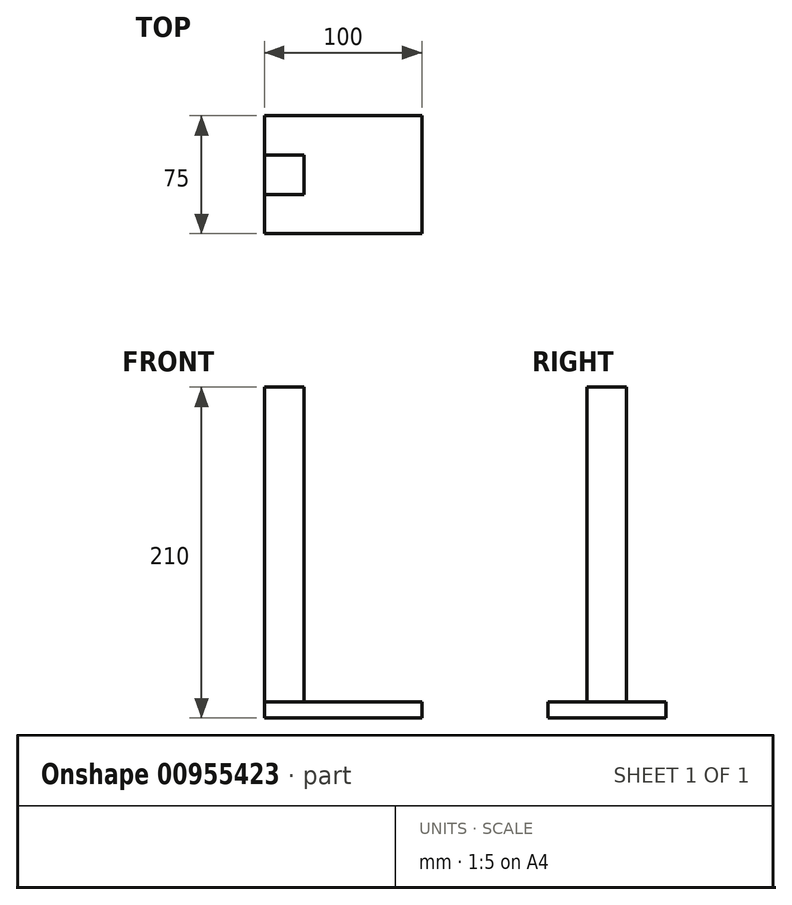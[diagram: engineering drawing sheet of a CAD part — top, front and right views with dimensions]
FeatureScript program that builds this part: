
annotation { "Feature Type Name" : "Feature", "Feature Type Description" : "" }
export const myFeature = defineFeature(function(context is Context, id is Id, definition is map)
    precondition{}
    {
        {
            var Q0;
            Q0=qCreatedBy(makeId("Top.planeOp"),FACE);
            var sketch = newSketch(context, id + "F0", { "sketchPlane" : qUnion([Q0])});
            skLineSegment(sketch, "E0.bottom", {"start": v(51.9, 49.62) * mm, "end": v(-48.1, 49.62) * mm});
            skLineSegment(sketch, "E0.top", {"start": v(51.9, -25.38) * mm, "end": v(-48.1, -25.38) * mm});
            skLineSegment(sketch, "E0.left", {"start": v(51.9, 49.62) * mm, "end": v(51.9, -25.38) * mm});
            skLineSegment(sketch, "E0.right", {"start": v(-48.1, 49.62) * mm, "end": v(-48.1, -25.38) * mm});
            skSolve(sketch);
        }
        {
            var Q0;
            Q0=makeQuery(id+"F0.imprint","IMPRINT",FACE,{"disambiguationData":[TD([[makeQuery(id+"F0.imprint","IMPRINT",EDGE,{"derivedFrom":sQuery(id+"F0.wireOp",EDGE,"E0.bottom")}),1.0]])]});
            extrude(context, id + "F1", {"entities" : qUnion([Q0]), "depth" : 10 * mm, "offsetDistance" : 25 * mm});
        }
        {
            var Q0;
            Q0=makeQuery(id+"F1.opExtrude","CAP_FACE",FACE,{"disambiguationData":[OSD([sQuery(id+"F0.wireOp",EDGE,"E0.bottom"),sQuery(id+"F0.wireOp",EDGE,"E0.top"),sQuery(id+"F0.wireOp",EDGE,"E0.left"),sQuery(id+"F0.wireOp",EDGE,"E0.right")])],"isStart":false});
            var sketch = newSketch(context, id + "F2", { "sketchPlane" : qUnion([Q0])});
            skLineSegment(sketch, "E1.bottom", {"start": v(-23.1, 24.62) * mm, "end": v(-48.1, 24.62) * mm});
            skLineSegment(sketch, "E1.top", {"start": v(-23.1, -0.38) * mm, "end": v(-48.1, -0.38) * mm});
            skLineSegment(sketch, "E1.left", {"start": v(-23.1, 24.62) * mm, "end": v(-23.1, -0.38) * mm});
            skLineSegment(sketch, "E1.right", {"start": v(-48.1, 24.62) * mm, "end": v(-48.1, -0.38) * mm});
            skPoint(sketch, "E1.middle", {"position": v(-35.6, 12.12) * mm});
            skPoint(sketch, "E1.middle.positionSnap0", {"position": v(-48.1, 12.12) * mm});
            skPoint(sketch, "E1.centerSnap0", {"position": v(-48.1, 12.12) * mm});
            skSolve(sketch);
        }
        {
            var Q0;
            Q0 = qSketchRegion(id + "F2", true);
            extrude(context, id + "F3", {"entities" : qUnion([Q0]), "operationType" : NewBodyOperationType.ADD, "depth" : 200 * mm, "offsetDistance" : 25 * mm});
        }
    });
